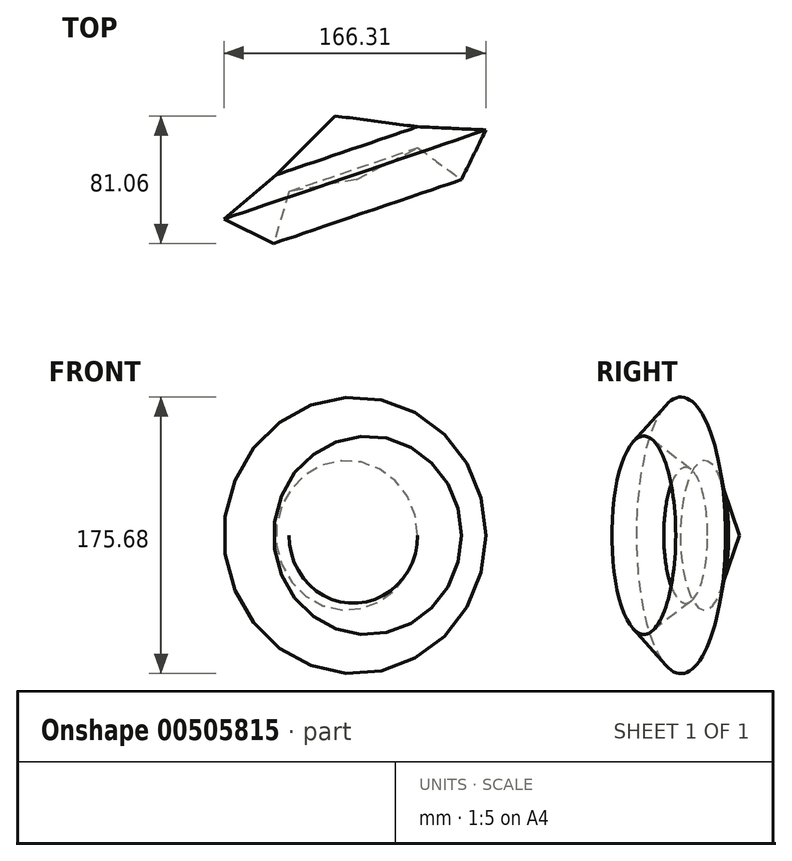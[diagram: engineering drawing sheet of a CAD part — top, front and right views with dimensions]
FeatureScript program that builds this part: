
annotation { "Feature Type Name" : "Feature", "Feature Type Description" : "" }
export const myFeature = defineFeature(function(context is Context, id is Id, definition is map)
    precondition{}
    {
        {
            var Q0;
            Q0=qCreatedBy(makeId("Top.planeOp"),FACE);
            var sketch = newSketch(context, id + "F0", { "sketchPlane" : qUnion([Q0])});
            skLineSegment(sketch, "E0", {"start": v(0, 0) * mm, "end": v(-38.73, -20.23) * mm});
            skLineSegment(sketch, "E1", {"start": v(0, 0) * mm, "end": v(27.83, -20.23) * mm});
            skLineSegment(sketch, "E2", {"start": v(27.83, -20.23) * mm, "end": v(43.32, 11.33) * mm});
            skLineSegment(sketch, "E3", {"start": v(-38.73, -20.23) * mm, "end": v(-52.5, 20.23) * mm});
            skLineSegment(sketch, "E4", {"start": v(-52.5, 20.23) * mm, "end": v(0, 13.34) * mm});
            skLineSegment(sketch, "E5", {"start": v(0, 13.34) * mm, "end": v(43.32, 11.33) * mm});
            skSolve(sketch);
        }
        {
            var Q0;
            Q0=makeQuery(id+"F0.imprint","IMPRINT",FACE,{"disambiguationData":[TD([[makeQuery(id+"F0.imprint","IMPRINT",EDGE,{"derivedFrom":sQuery(id+"F0.wireOp",EDGE,"E0")}),-1.0]])]});
            var Q1;
            Q1=sQuery(id+"F0.wireOp",EDGE,"E3");
            revolve(context, id + "F1", {"entities" : qUnion([Q0]), "axis" : qUnion([Q1]), "revolveType" : RevolveType.FULL});
        }
    });
